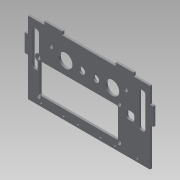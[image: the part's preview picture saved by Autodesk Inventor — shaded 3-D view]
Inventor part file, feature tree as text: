
AUTODESK INVENTOR PART (.ipt)
format: ipt  version: 2015 SP1 (Build 190203100, 203)  size: 917,504 bytes
history: native  units: mm
features: extrude x5, sketch x3, fillet x1
ambient origin geometry x8: Origin, YZ Plane, XZ Plane, XY Plane, X Axis, Y Axis, Z Axis, Center Point
bodies: Solid1 (feature_tree)
feature tree (9):
  sketch  "Sketch1"  dims[d20=6.0mm d21=0.0mm]
  extrude  "Extrusion1"  TaperAngle=0.0deg  [1 undecoded]
  sketch  "Sketch2"  dims[d22=7.353mm d23=1.598861mm]
  extrude  "Extrusion3"  Depth=1.598861mm
  extrude  "Extrusion4"  Depth=1.5mm
  extrude  "Extrusion5"  Depth=1.5mm
  extrude  "Extrusion6"  Depth=1.5mm
  fillet  "Fillet2"  Radius=6.0mm
  sketch  "Sketch3"  dims[d27=43.688mm d28=21.844mm d30=3.1mm d32=11.75mm d33=6.0mm d34=6.604mm d35=6.604mm d38=13.691mm d41=2.0mm d42=0.0mm d45=70.0mm d46=1.598861mm d47=1.598861mm d48=2.0mm d49=0.0mm d52=7.5mm d53=2.0mm d59=2.0mm d60=0.0mm d61=26.0mm d62=71.7mm d63=31.2mm d64=75.25mm d67=2.6mm d70=1.775mm d71=10.4mm d72=1.0mm d73=0.0mm d74=0.891933mm d75=1.0mm d76=0.0mm d77=1.5mm]
note: 1 required parameter value undecoded (feature->parameter linkage not recoverable at this tier; creation-order binding heuristic only, values carry confidence <= 0.55)
